# Revit family: DC_Holyoake_OutsideLouver_OHL-C-124_supply_13
name_source: partatom
category: Air Terminals
revit_build: Autodesk Revit 2014 (Build: 20130308_1515(x64)
units: mm (PartAtom-declared; Revit-internal decimal feet)

## types (1)
- OHL-C-124
    Accessories = Aluminium Bird mesh or insect mesh (fibreglass)
    Blade Array Count = 10.094488
    Blade Count = 9
    Blade Cut Setout = 685.8 mm
    Blade Height = 89.8 mm
    Blade Length = 709.2 mm  [stored 2.32677 ft]
    Blade Offset = 3.05 mm
    Blade Pitch = 76.2 mm  [stored 0.25 ft]
    Blade Width = 97.1 mm  [stored 0.31857 ft]
    Channel Thickness = 103.2 mm  [stored 0.338583 ft]
    Channel Width = 25.4 mm  [stored 0.0833333 ft]
    Connector Height = 745.2 mm
    Connector Width = 685.2 mm  [stored 2.24803 ft]
    Description = Weather Louvres shall be Holyoake Model OHL-C-124 straight profile 76mm louvred blades set at 76mm centres and constructed in a channel (C) frame to suit the installation profile.  Weather Louvres shall be of extruded aluminium construction and finished in natural anodised or powdercoat and fitted with accessories and dampers where indicated as manufactured by Holyoake.
    Exact Neck Height = 820 mm  [stored 2.69029 ft]
    Exact Neck Width = 760 mm  [stored 2.49344 ft]
    Holyoake Product Range = Outside Louvres
    Manufacturer = Holyoake
    Material - Body = Holyoake Aluminium
    Material - Face = Holyoake Aluminium
    Max Flow = 2000.0 L/s
    Min Flow = 100.0 L/s
    Model = OHL-C-124
    Noise Level NC Max = 0.00 NC
    Noise Level NC Min = 0.00 NC
    Nominal Height = 826 mm  [stored 2.70997 ft]
    Nominal Width = 766 mm  [stored 2.51312 ft]
    Overall Depth = 38.3 mm  [stored 0.125656 ft]
    Overall Opening = 769.2 mm  [stored 2.52362 ft]
    Static Pressure Max = 0.0 Pa
    Static Pressure Min = 0.0 Pa
    Top Blade Height = 83.4 mm
    Type Comments = 76mm Horizontal Straight Profile Louvers in Channel Surround
    URL = http://www.holyoake.com

note: [stored X ft] marks values corroborated as IEEE doubles in the binary element streams (Revit-internal decimal feet)

## geometry (parser evidence)
native form markers: Blend x6, Sweep x12
no freeform markers — native parametric forms only
